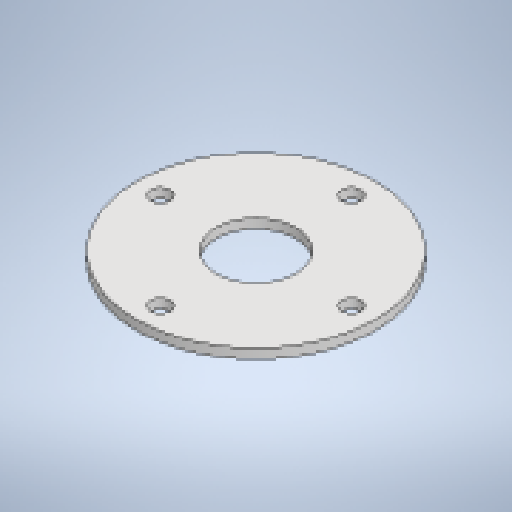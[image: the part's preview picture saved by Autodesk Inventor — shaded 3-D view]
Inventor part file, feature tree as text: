
AUTODESK INVENTOR PART (.ipt)
format: ipt  version: 2025 (Build 290162010, 162A)  size: 255,488 bytes
history: native  units: mm
features: other x5, sketch x3, sheet_metal_op x1, pattern_circular x1, projected_geometry x1
ambient origin geometry x8: Origin, YZ Plane, XZ Plane, XY Plane, X Axis, Y Axis, Z Axis, Center Point
bodies: Solid1 (feature_tree)
feature tree (11):
  sheet_metal_op  "Face1"
  other  "Mark1"
  other  "A-Side Definition"
  pattern_circular  "Circular Pattern1"  Count=20  [1 undecoded]
  sketch  "Sketch1"  dims[d2=3.0mm d6=200.0mm]
  other  "Plate1"
  sketch  "Sketch2"  dims[d9=20.0mm]
  sketch  "Sketch3"  dims[d15=25.0mm d16=75.0mm d17=6.0mm d19=7.5mm d20=3.0mm d21=0.0mm d22=40.0mm d23=360.0deg d26=60.0mm]
  projected_geometry  "Projected Loop1"
  other  "Cut1"
  other  "Definition1"
note: 1 required parameter value undecoded (feature->parameter linkage not recoverable at this tier; creation-order binding heuristic only, values carry confidence <= 0.55)
